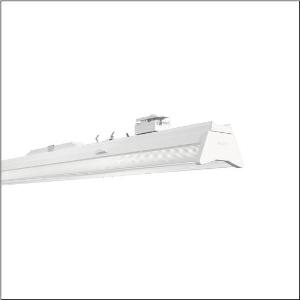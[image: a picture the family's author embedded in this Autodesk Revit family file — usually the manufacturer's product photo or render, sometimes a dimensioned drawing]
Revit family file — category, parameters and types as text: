
# Revit family: licross_r__21_performance_mo_52tm16cn49xg_ab5a
name_source: partatom
category: Lighting Fixtures
units: mm (PartAtom-declared; Revit-internal decimal feet)

## family parameters
Cut with Voids When Loaded = No
Host = Face
Light Source = No
Part Type = Normal
Room Calculation Point = No
Round Connector Dimension = Use Diameter
Shared = No

## types (1)
- --- (1 x LED, 9240 lm, 50.4 W, 4000K)
    Apparent Load = 50 VA
    CIE Flux Codes = 66 88 96 79 100
    Color Rendering = 80
    Color Temperature = 4000K
    Default Elevation = 1800 mm
    Description = Licross® 21 Performance MO, luminaire insert, of sheet steel, galvanised, coil coated, white, length: 1.500mm, width: 120mm, height: 123mm, LED rated luminous flux: 9.240lm, light colour: 840, control gear: ON/OFF Multilumen, CLOi, control gear: ECG Multilumen, with plug, 3-pole, with phase selection, mains connection: 220..240V, AC, 50/60Hz, start of lifetime: 50W, end of service life: 61W, halogen-free wiring, primary light control with lens, of plastic, primary optical cover: cover, of PMMA, light emission: direct/indirect distribution, primary light characteristic: symmetric, protection rating (complete): IP40, insulation class (complete): insulation class I (protective earthing), certification: CE, ENEC, UKCA, protection symbol: D if used in an environment without relevant dust loads with corresponding accessories, impact resistance: IK06, permissible ambient temperature for indoor applications: -35..+45°C, corresponds to IFS (International Featured Standards) requirements for safety and quality in the food industry, reducing of maximum allowable ambient temperature of 5°C with ceiling mounting, LABS conformity tested according to VDMA 24364:2018-05, packaging unit: 1 piece
    Height = 114 mm
    Lamp = 1 x LED
    Lamp Light Flux = 9240 lm
    Lamp Power = 50.4 W
    Lamp count = 1
    Length = 1500 mm
    Luminous efficacy = 183 lm/W
    Manufacturer = Siteco
    ModVariant = No
    Model = 52TM16CN49XG
    Mounting Place = Ceiling
    Mounting Type = Pendant
    Number of Poles = 1
    OnlyDefault = Yes
    Power Factor = 1
    Product Name = Licross® 21 Performance MO
    Product group = luminaire insert
    ProductGroupID = 901
    Protection Class = Protection class I
    Protection Degree = IP 40
    RLX_Detail_Level = 1
    RLX_Emergency_Light_Flux = 0 lm
    RLX_Emergency_Type = 0
    RLX_Emergency_Type_DB = No
    RlxData = <blob elided: 31829 chars, md5=37b8f0cb>
    Socket = socket
    Standby Power = 0 W
    System Light Flux = 9240 lm
    System Power = 50 W
    Type Comments = factory setting: luminous flux: 100 % | (A | C | E) | 117 mA
    Type Image = l_1256138.jpg
    URL = http://relux.com
    VarID = @adj_059839
    Voltage = 0 V
    Weight = 0.00 kg
    Width = 120 mm

## geometry (parser evidence)
native form markers: Blend x4, Sweep x14
no freeform markers — native parametric forms only
